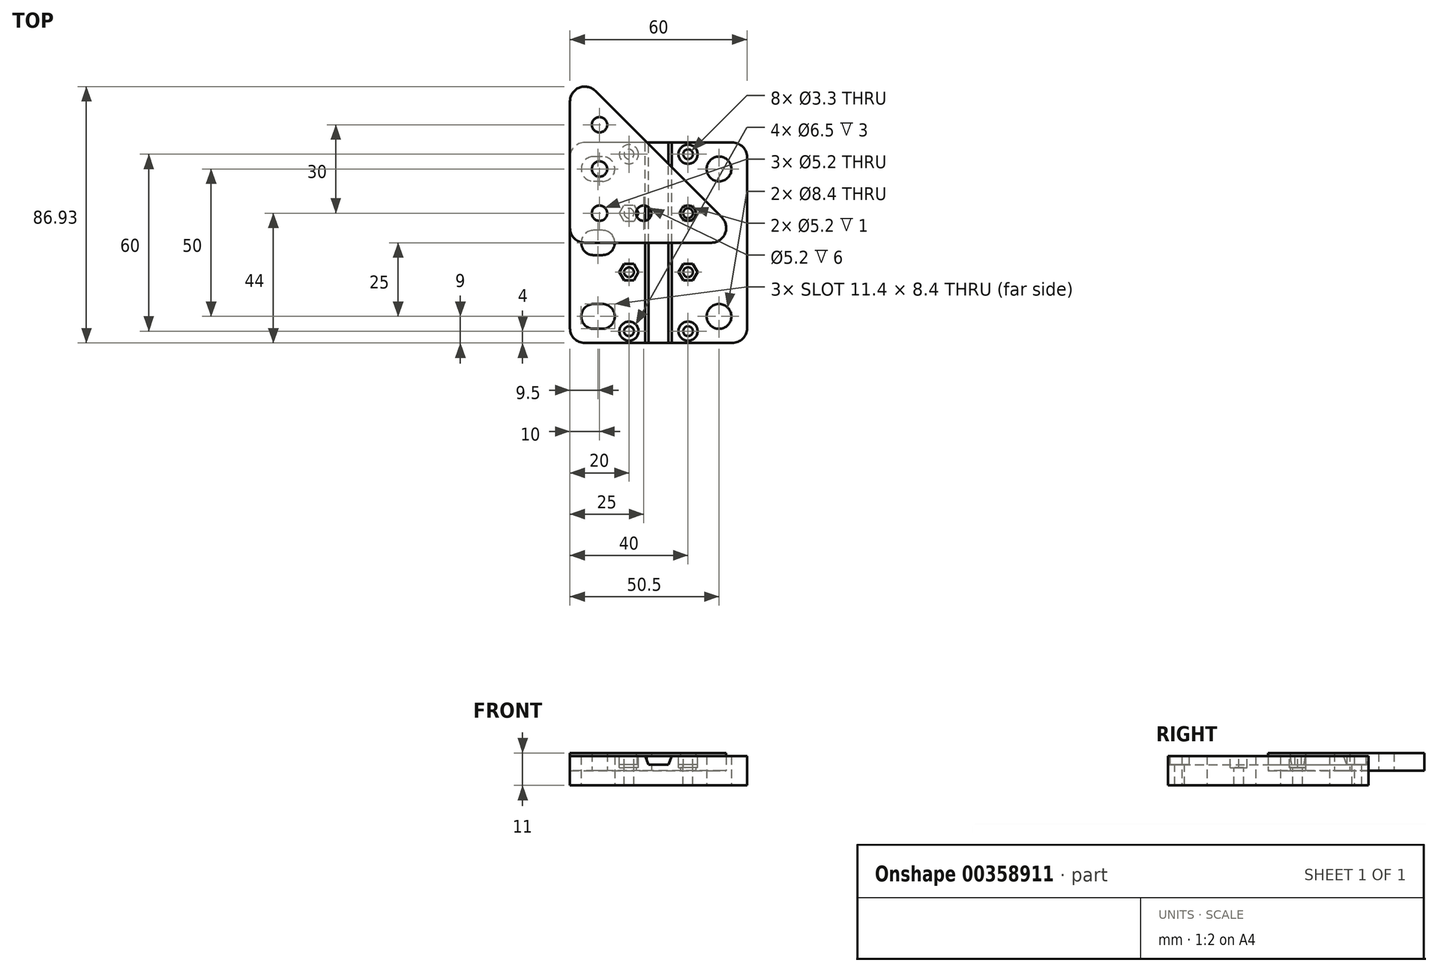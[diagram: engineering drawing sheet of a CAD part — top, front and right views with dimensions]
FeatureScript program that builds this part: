
annotation { "Feature Type Name" : "Feature", "Feature Type Description" : "" }
export const myFeature = defineFeature(function(context is Context, id is Id, definition is map)
    precondition{}
    {
        {
            var Q0;
            Q0=qCreatedBy(makeId("Top.planeOp"),FACE);
            var sketch = newSketch(context, id + "F0", { "sketchPlane" : qUnion([Q0])});
            skLineSegment(sketch, "E0", {"start": v(-30, 0) * mm, "end": v(30, 0) * mm});
            skLineSegment(sketch, "E1", {"start": v(30, 0) * mm, "end": v(-30, 60) * mm});
            skLineSegment(sketch, "E2", {"start": v(-30, 60) * mm, "end": v(-30, 0) * mm});
            skCircle(sketch, "E3", {"center": v(-20, 10) * mm, "radius": 2.6 * mm});
            skCircle(sketch, "E4.0.1.0", {"center": v(-20, 25) * mm, "radius": 2.6 * mm});
            skCircle(sketch, "E4.0.2.0", {"center": v(-20, 40) * mm, "radius": 2.6 * mm});
            skCircle(sketch, "E4.1.0.0", {"center": v(-5, 10) * mm, "radius": 2.6 * mm});
            skCircle(sketch, "E4.2.0.0", {"center": v(10, 10) * mm, "radius": 2.6 * mm});
            skLineSegment(sketch, "E4.direction1", {"start": v(-20, 10) * mm, "end": v(-5, 10) * mm, "construction": true});
            skLineSegment(sketch, "E4.direction2", {"start": v(-20, 10) * mm, "end": v(-20, 25) * mm, "construction": true});
            skLineSegment(sketch, "E5", {"start": v(-20, 10) * mm, "end": v(-30, 10) * mm, "construction": true});
            skLineSegment(sketch, "E6", {"start": v(-20, 10) * mm, "end": v(-20, 0) * mm, "construction": true});
            skSolve(sketch);
        }
        {
            var Q0;
            Q0=makeQuery(id+"F0.imprint","IMPRINT",FACE,{"disambiguationData":[TD([[makeQuery(id+"F0.imprint","IMPRINT",EDGE,{"derivedFrom":sQuery(id+"F0.wireOp",EDGE,"E0")}),1.0]])]});
            extrude(context, id + "F1", {"entities" : qUnion([Q0]), "depth" : 6 * mm});
        }
        {
            var Q0;
            Q0=makeQuery(id+"F1.opExtrude","SWEPT_EDGE",EDGE,{"disambiguationData":[OSD([sQuery(id+"F0.wireOp",EDGE,"E0"),sQuery(id+"F0.wireOp",EDGE,"E2")])]});
            var Q1;
            Q1=makeQuery(id+"F1.opExtrude","SWEPT_EDGE",EDGE,{"disambiguationData":[OSD([sQuery(id+"F0.wireOp",EDGE,"E0"),sQuery(id+"F0.wireOp",EDGE,"E1")])]});
            var Q2;
            Q2=makeQuery(id+"F1.opExtrude","SWEPT_EDGE",EDGE,{"disambiguationData":[OSD([sQuery(id+"F0.wireOp",EDGE,"E1"),sQuery(id+"F0.wireOp",EDGE,"E2")])]});
            fillet(context, id + "F2", {"entities" : qUnion([Q0, Q1, Q2]), "radius" : 5 * mm, "tangentPropagation" : true, "allowEdgeOverflow" : false});
        }
        {
            var Q0;
            Q0=qCreatedBy(makeId("Top.planeOp"),FACE);
            var sketch = newSketch(context, id + "F3", { "sketchPlane" : qUnion([Q0])});
            skLineSegment(sketch, "E7.bottom", {"start": v(30, 34) * mm, "end": v(-30, 34) * mm});
            skLineSegment(sketch, "E7.top", {"start": v(30, -34) * mm, "end": v(-30, -34) * mm});
            skLineSegment(sketch, "E7.left", {"start": v(30, 34) * mm, "end": v(30, -34) * mm});
            skLineSegment(sketch, "E7.right", {"start": v(-30, 34) * mm, "end": v(-30, -34) * mm});
            skPoint(sketch, "E7.middle", {"position": v(0, 0) * mm});
            skPoint(sketch, "E8.middle", {"position": v(-30, 34) * mm});
            skCircle(sketch, "E9", {"center": v(20.5, 0) * mm, "radius": 11 * mm, "construction": true});
            skLineSegment(sketch, "E10", {"start": v(20.5, -34) * mm, "end": v(20.5, 34) * mm, "construction": true});
            skCircle(sketch, "E11", {"center": v(20.5, 25) * mm, "radius": 4.2 * mm});
            skCircle(sketch, "E12.0.1.0", {"center": v(20.5, -25) * mm, "radius": 4.2 * mm});
            skLineSegment(sketch, "E12.direction1", {"start": v(20.5, 25) * mm, "end": v(-14.9, 25) * mm, "construction": true});
            skLineSegment(sketch, "E12.direction2", {"start": v(20.5, 25) * mm, "end": v(20.5, -25) * mm, "construction": true});
            skLineSegment(sketch, "E13", {"start": v(-20.5, 34) * mm, "end": v(-20.5, -34) * mm, "construction": true});
            skLineSegment(sketch, "E14.bottom", {"start": v(-19, -29.2) * mm, "end": v(-22, -29.2) * mm});
            skLineSegment(sketch, "E14.top", {"start": v(-19, -20.8) * mm, "end": v(-22, -20.8) * mm});
            skLineSegment(sketch, "E14.left", {"start": v(-19, -29.2) * mm, "end": v(-19, -20.8) * mm});
            skLineSegment(sketch, "E14.right", {"start": v(-22, -29.2) * mm, "end": v(-22, -20.8) * mm});
            skPoint(sketch, "E14.middle", {"position": v(-20.5, -25) * mm});
            skArc(sketch, "E15", {"start": v(-22, -29.2) * mm, "mid": v(-26.2, -25) * mm, "end": v(-22, -20.8) * mm});
            skArc(sketch, "E16", {"start": v(-19, -29.2) * mm, "mid": v(-14.8, -25) * mm, "end": v(-19, -20.8) * mm});
            skLineSegment(sketch, "E17.0.1.0", {"start": v(-19, -4.2) * mm, "end": v(-22, -4.2) * mm});
            skLineSegment(sketch, "E17.0.1.1", {"start": v(-19, 4.2) * mm, "end": v(-22, 4.2) * mm});
            skArc(sketch, "E17.0.1.2", {"start": v(-19, -4.2) * mm, "mid": v(-14.8, 0) * mm, "end": v(-19, 4.2) * mm});
            skArc(sketch, "E17.0.1.3", {"start": v(-22, -4.2) * mm, "mid": v(-26.2, 0) * mm, "end": v(-22, 4.2) * mm});
            skLineSegment(sketch, "E17.0.1.4", {"start": v(-22, -4.2) * mm, "end": v(-22, 4.2) * mm});
            skLineSegment(sketch, "E17.0.1.5", {"start": v(-19, -4.2) * mm, "end": v(-19, 4.2) * mm});
            skPoint(sketch, "E17.0.1.6", {"position": v(-20.5, 0) * mm});
            skLineSegment(sketch, "E17.0.2.0", {"start": v(-19, 20.8) * mm, "end": v(-22, 20.8) * mm});
            skLineSegment(sketch, "E17.0.2.1", {"start": v(-19, 29.2) * mm, "end": v(-22, 29.2) * mm});
            skArc(sketch, "E17.0.2.2", {"start": v(-19, 20.8) * mm, "mid": v(-14.8, 25) * mm, "end": v(-19, 29.2) * mm});
            skArc(sketch, "E17.0.2.3", {"start": v(-22, 20.8) * mm, "mid": v(-26.2, 25) * mm, "end": v(-22, 29.2) * mm});
            skLineSegment(sketch, "E17.0.2.4", {"start": v(-22, 20.8) * mm, "end": v(-22, 29.2) * mm});
            skLineSegment(sketch, "E17.0.2.5", {"start": v(-19, 20.8) * mm, "end": v(-19, 29.2) * mm});
            skPoint(sketch, "E17.0.2.6", {"position": v(-20.5, 25) * mm});
            skLineSegment(sketch, "E17.direction1", {"start": v(-22, -29.2) * mm, "end": v(3.25, -29.2) * mm, "construction": true});
            skLineSegment(sketch, "E17.direction2", {"start": v(-22, -29.2) * mm, "end": v(-22, -4.2) * mm, "construction": true});
            skSolve(sketch);
        }
        {
            var Q0;
            Q0=makeQuery(id+"F3.imprint","IMPRINT",FACE,{"disambiguationData":[TD([[makeQuery(id+"F3.imprint","IMPRINT",EDGE,{"derivedFrom":sQuery(id+"F3.wireOp",EDGE,"E7.bottom")}),1.0]])]});
            extrude(context, id + "F4", {"entities" : qUnion([Q0]), "endBound" : BoundingType.SYMMETRIC, "depth" : 10 * mm});
        }
        {
            var Q0;
            Q0=makeQuery(id+"F4.opExtrude","SWEPT_EDGE",EDGE,{"disambiguationData":[OSD([sQuery(id+"F3.wireOp",EDGE,"E7.bottom"),sQuery(id+"F3.wireOp",EDGE,"E7.right")])]});
            var Q1;
            Q1=makeQuery(id+"F4.opExtrude","SWEPT_EDGE",EDGE,{"disambiguationData":[OSD([sQuery(id+"F3.wireOp",EDGE,"E7.top"),sQuery(id+"F3.wireOp",EDGE,"E7.right")])]});
            var Q2;
            Q2=makeQuery(id+"F4.opExtrude","SWEPT_EDGE",EDGE,{"disambiguationData":[OSD([sQuery(id+"F3.wireOp",EDGE,"E7.top"),sQuery(id+"F3.wireOp",EDGE,"E7.left")])]});
            var Q3;
            Q3=makeQuery(id+"F4.opExtrude","SWEPT_EDGE",EDGE,{"disambiguationData":[OSD([sQuery(id+"F3.wireOp",EDGE,"E7.bottom"),sQuery(id+"F3.wireOp",EDGE,"E7.left")])]});
            fillet(context, id + "F5", {"entities" : qUnion([Q0, Q1, Q2, Q3]), "radius" : 5 * mm, "tangentPropagation" : true, "allowEdgeOverflow" : false});
        }
        {
            var Q0;
            Q0=makeQuery(id+"F4.opExtrude","CAP_FACE",FACE,{"disambiguationData":[OSD([sQuery(id+"F3.wireOp",EDGE,"E7.bottom"),sQuery(id+"F3.wireOp",EDGE,"E7.top"),sQuery(id+"F3.wireOp",EDGE,"E7.left"),sQuery(id+"F3.wireOp",EDGE,"E7.right"),sQuery(id+"F3.wireOp",EDGE,"E11"),sQuery(id+"F3.wireOp",EDGE,"E12.0.1.0"),sQuery(id+"F3.wireOp",EDGE,"E14.bottom"),sQuery(id+"F3.wireOp",EDGE,"E14.top"),sQuery(id+"F3.wireOp",EDGE,"E15"),sQuery(id+"F3.wireOp",EDGE,"E16"),sQuery(id+"F3.wireOp",EDGE,"E17.0.1.0"),sQuery(id+"F3.wireOp",EDGE,"E17.0.1.1"),sQuery(id+"F3.wireOp",EDGE,"E17.0.1.2"),sQuery(id+"F3.wireOp",EDGE,"E17.0.1.3"),sQuery(id+"F3.wireOp",EDGE,"E17.0.2.0"),sQuery(id+"F3.wireOp",EDGE,"E17.0.2.1"),sQuery(id+"F3.wireOp",EDGE,"E17.0.2.2"),sQuery(id+"F3.wireOp",EDGE,"E17.0.2.3")])],"isStart":false});
            var sketch = newSketch(context, id + "F6", { "sketchPlane" : qUnion([Q0])});
            skCircle(sketch, "E18", {"center": v(-10, -30) * mm, "radius": 1.6 * mm});
            skCircle(sketch, "E19.0.1.0", {"center": v(-10, 30) * mm, "radius": 1.6 * mm});
            skCircle(sketch, "E19.1.0.0", {"center": v(10, -30) * mm, "radius": 1.6 * mm});
            skCircle(sketch, "E19.1.1.0", {"center": v(10, 30) * mm, "radius": 1.6 * mm});
            skLineSegment(sketch, "E19.direction1", {"start": v(-10, -30) * mm, "end": v(10, -30) * mm, "construction": true});
            skLineSegment(sketch, "E19.direction2", {"start": v(-10, -30) * mm, "end": v(-10, 30) * mm, "construction": true});
            skSolve(sketch);
        }
        {
            var Q0;
            Q0=sQuery(id+"F6.wireOp",VERTEX,"E19.0.1.0.center");
            var Q1;
            Q1=sQuery(id+"F6.wireOp",VERTEX,"E19.1.1.0.center");
            var Q2;
            Q2=sQuery(id+"F6.wireOp",VERTEX,"E18.center");
            var Q3;
            Q3=sQuery(id+"F6.wireOp",VERTEX,"E19.1.0.0.center");
            var Q4;
            Q4=makeQuery(id+"F4.opExtrude","SWEPT_BODY",BODY,{"disambiguationData":[OSD([sQuery(id+"F3.wireOp",EDGE,"E7.bottom"),sQuery(id+"F3.wireOp",EDGE,"E7.top"),sQuery(id+"F3.wireOp",EDGE,"E7.left"),sQuery(id+"F3.wireOp",EDGE,"E7.right"),sQuery(id+"F3.wireOp",EDGE,"E11"),sQuery(id+"F3.wireOp",EDGE,"E12.0.1.0"),sQuery(id+"F3.wireOp",EDGE,"E14.bottom"),sQuery(id+"F3.wireOp",EDGE,"E14.top"),sQuery(id+"F3.wireOp",EDGE,"E15"),sQuery(id+"F3.wireOp",EDGE,"E16"),sQuery(id+"F3.wireOp",EDGE,"E17.0.1.0"),sQuery(id+"F3.wireOp",EDGE,"E17.0.1.1"),sQuery(id+"F3.wireOp",EDGE,"E17.0.1.2"),sQuery(id+"F3.wireOp",EDGE,"E17.0.1.3"),sQuery(id+"F3.wireOp",EDGE,"E17.0.2.0"),sQuery(id+"F3.wireOp",EDGE,"E17.0.2.1"),sQuery(id+"F3.wireOp",EDGE,"E17.0.2.2"),sQuery(id+"F3.wireOp",EDGE,"E17.0.2.3")])]});
            hole(context, id + "F7", {"style" : HoleStyle.C_BORE, "endStyle" : HoleEndStyle.THROUGH, "standardTappedOrClearance" : lookupTablePath({ "standard" : "ISO", "fit" : "Normal", "size" : "M3", "type" : "Clearance" }), "standardBlindInLast" : lookupTablePath({ "fit" : "Standard", "standard" : "ISO", "size" : "M3", "type" : "Clearance" }), "holeDiameter" : 3.3 * mm, "cBoreDiameter" : 6.5 * mm, "cBoreDepth" : 3 * mm, "isTappedThrough" : true, "tappedDepth" : 12 * mm, "tapClearance" : 3, "startFromSketch" : true, "locations" : qUnion([Q0, Q1, Q2, Q3]), "scope" : qUnion([Q4])});
        }
        {
            var Q0;
            Q0=makeQuery(id+"F4.opExtrude","CAP_FACE",FACE,{"disambiguationData":[OSD([sQuery(id+"F3.wireOp",EDGE,"E7.bottom"),sQuery(id+"F3.wireOp",EDGE,"E7.top"),sQuery(id+"F3.wireOp",EDGE,"E7.left"),sQuery(id+"F3.wireOp",EDGE,"E7.right"),sQuery(id+"F3.wireOp",EDGE,"E11"),sQuery(id+"F3.wireOp",EDGE,"E12.0.1.0"),sQuery(id+"F3.wireOp",EDGE,"E14.bottom"),sQuery(id+"F3.wireOp",EDGE,"E14.top"),sQuery(id+"F3.wireOp",EDGE,"E15"),sQuery(id+"F3.wireOp",EDGE,"E16"),sQuery(id+"F3.wireOp",EDGE,"E17.0.1.0"),sQuery(id+"F3.wireOp",EDGE,"E17.0.1.1"),sQuery(id+"F3.wireOp",EDGE,"E17.0.1.2"),sQuery(id+"F3.wireOp",EDGE,"E17.0.1.3"),sQuery(id+"F3.wireOp",EDGE,"E17.0.2.0"),sQuery(id+"F3.wireOp",EDGE,"E17.0.2.1"),sQuery(id+"F3.wireOp",EDGE,"E17.0.2.2"),sQuery(id+"F3.wireOp",EDGE,"E17.0.2.3")])],"isStart":false});
            var sketch = newSketch(context, id + "F8", { "sketchPlane" : qUnion([Q0])});
            skCircle(sketch, "E20.cCircle", {"center": v(-10, -10) * mm, "radius": 3.25 * mm, "construction": true});
            skLineSegment(sketch, "E20.0", {"start": v(-6.75, -10) * mm, "end": v(-8.38, -12.81) * mm});
            skLineSegment(sketch, "E20.1", {"start": v(-8.38, -12.81) * mm, "end": v(-11.62, -12.81) * mm});
            skLineSegment(sketch, "E20.2", {"start": v(-11.62, -12.81) * mm, "end": v(-13.25, -10) * mm});
            skLineSegment(sketch, "E20.3", {"start": v(-13.25, -10) * mm, "end": v(-11.62, -7.19) * mm});
            skLineSegment(sketch, "E20.4", {"start": v(-11.62, -7.19) * mm, "end": v(-8.37, -7.19) * mm});
            skLineSegment(sketch, "E20.5", {"start": v(-8.37, -7.19) * mm, "end": v(-6.75, -10) * mm});
            skLineSegment(sketch, "E21.0.1.0", {"start": v(-13.25, 10) * mm, "end": v(-11.62, 12.81) * mm});
            skLineSegment(sketch, "E21.0.1.1", {"start": v(-11.62, 7.19) * mm, "end": v(-13.25, 10) * mm});
            skLineSegment(sketch, "E21.0.1.2", {"start": v(-8.38, 7.19) * mm, "end": v(-11.62, 7.19) * mm});
            skLineSegment(sketch, "E21.0.1.3", {"start": v(-6.75, 10) * mm, "end": v(-8.38, 7.19) * mm});
            skCircle(sketch, "E21.0.1.4", {"center": v(-10, 10) * mm, "radius": 3.25 * mm, "construction": true});
            skLineSegment(sketch, "E21.0.1.5", {"start": v(-8.37, 12.81) * mm, "end": v(-6.75, 10) * mm});
            skLineSegment(sketch, "E21.0.1.6", {"start": v(-11.62, 12.81) * mm, "end": v(-8.37, 12.81) * mm});
            skLineSegment(sketch, "E21.1.0.0", {"start": v(6.75, -10) * mm, "end": v(8.38, -7.19) * mm});
            skLineSegment(sketch, "E21.1.0.1", {"start": v(8.38, -12.81) * mm, "end": v(6.75, -10) * mm});
            skLineSegment(sketch, "E21.1.0.2", {"start": v(11.62, -12.81) * mm, "end": v(8.38, -12.81) * mm});
            skLineSegment(sketch, "E21.1.0.3", {"start": v(13.25, -10) * mm, "end": v(11.62, -12.81) * mm});
            skCircle(sketch, "E21.1.0.4", {"center": v(10, -10) * mm, "radius": 3.25 * mm, "construction": true});
            skLineSegment(sketch, "E21.1.0.5", {"start": v(11.63, -7.19) * mm, "end": v(13.25, -10) * mm});
            skLineSegment(sketch, "E21.1.0.6", {"start": v(8.38, -7.19) * mm, "end": v(11.63, -7.19) * mm});
            skLineSegment(sketch, "E21.1.1.0", {"start": v(6.75, 10) * mm, "end": v(8.38, 12.81) * mm});
            skLineSegment(sketch, "E21.1.1.1", {"start": v(8.38, 7.19) * mm, "end": v(6.75, 10) * mm});
            skLineSegment(sketch, "E21.1.1.2", {"start": v(11.62, 7.19) * mm, "end": v(8.38, 7.19) * mm});
            skLineSegment(sketch, "E21.1.1.3", {"start": v(13.25, 10) * mm, "end": v(11.62, 7.19) * mm});
            skCircle(sketch, "E21.1.1.4", {"center": v(10, 10) * mm, "radius": 3.25 * mm, "construction": true});
            skLineSegment(sketch, "E21.1.1.5", {"start": v(11.63, 12.81) * mm, "end": v(13.25, 10) * mm});
            skLineSegment(sketch, "E21.1.1.6", {"start": v(8.38, 12.81) * mm, "end": v(11.63, 12.81) * mm});
            skLineSegment(sketch, "E21.direction1", {"start": v(-11.62, -12.81) * mm, "end": v(8.38, -12.81) * mm, "construction": true});
            skLineSegment(sketch, "E21.direction2", {"start": v(-11.62, -12.81) * mm, "end": v(-11.62, 7.19) * mm, "construction": true});
            skSolve(sketch);
        }
        {
            var Q0;
            Q0=makeQuery(id+"F8.imprint","IMPRINT",FACE,{"disambiguationData":[TD([[makeQuery(id+"F8.imprint","IMPRINT",EDGE,{"derivedFrom":sQuery(id+"F8.wireOp",EDGE,"E21.0.1.0")}),-1.0]])]});
            var Q1;
            Q1=makeQuery(id+"F8.imprint","IMPRINT",FACE,{"disambiguationData":[TD([[makeQuery(id+"F8.imprint","IMPRINT",EDGE,{"derivedFrom":sQuery(id+"F8.wireOp",EDGE,"E21.1.1.0")}),-1.0]])]});
            var Q2;
            Q2=makeQuery(id+"F8.imprint","IMPRINT",FACE,{"disambiguationData":[TD([[makeQuery(id+"F8.imprint","IMPRINT",EDGE,{"derivedFrom":sQuery(id+"F8.wireOp",EDGE,"E20.0")}),-1.0]])]});
            var Q3;
            Q3=makeQuery(id+"F8.imprint","IMPRINT",FACE,{"disambiguationData":[TD([[makeQuery(id+"F8.imprint","IMPRINT",EDGE,{"derivedFrom":sQuery(id+"F8.wireOp",EDGE,"E21.1.0.0")}),-1.0]])]});
            extrude(context, id + "F9", {"entities" : qUnion([Q0, Q1, Q2, Q3]), "operationType" : NewBodyOperationType.REMOVE, "oppositeDirection" : true, "depth" : 4 * mm});
        }
        {
            var Q0;
            Q0=sQuery(id+"F8.wireOp",VERTEX,"E21.0.1.4.center");
            var Q1;
            Q1=sQuery(id+"F8.wireOp",VERTEX,"E21.1.1.4.center");
            var Q2;
            Q2=sQuery(id+"F8.wireOp",VERTEX,"E20.cCircle.center");
            var Q3;
            Q3=sQuery(id+"F8.wireOp",VERTEX,"E21.1.0.4.center");
            var Q4;
            Q4=makeQuery(id+"F4.opExtrude","SWEPT_BODY",BODY,{"disambiguationData":[OSD([sQuery(id+"F3.wireOp",EDGE,"E7.bottom"),sQuery(id+"F3.wireOp",EDGE,"E7.top"),sQuery(id+"F3.wireOp",EDGE,"E7.left"),sQuery(id+"F3.wireOp",EDGE,"E7.right"),sQuery(id+"F3.wireOp",EDGE,"E11"),sQuery(id+"F3.wireOp",EDGE,"E12.0.1.0"),sQuery(id+"F3.wireOp",EDGE,"E14.bottom"),sQuery(id+"F3.wireOp",EDGE,"E14.top"),sQuery(id+"F3.wireOp",EDGE,"E15"),sQuery(id+"F3.wireOp",EDGE,"E16"),sQuery(id+"F3.wireOp",EDGE,"E17.0.1.0"),sQuery(id+"F3.wireOp",EDGE,"E17.0.1.1"),sQuery(id+"F3.wireOp",EDGE,"E17.0.1.2"),sQuery(id+"F3.wireOp",EDGE,"E17.0.1.3"),sQuery(id+"F3.wireOp",EDGE,"E17.0.2.0"),sQuery(id+"F3.wireOp",EDGE,"E17.0.2.1"),sQuery(id+"F3.wireOp",EDGE,"E17.0.2.2"),sQuery(id+"F3.wireOp",EDGE,"E17.0.2.3")])]});
            hole(context, id + "F10", {"style" : HoleStyle.SIMPLE, "endStyle" : HoleEndStyle.THROUGH, "standardTappedOrClearance" : lookupTablePath({ "standard" : "ISO", "fit" : "Normal", "size" : "M3", "type" : "Clearance" }), "standardBlindInLast" : lookupTablePath({ "fit" : "Standard", "standard" : "ISO", "size" : "M3", "type" : "Clearance" }), "holeDiameter" : 3.3 * mm, "isTappedThrough" : true, "tappedDepth" : 12 * mm, "tapClearance" : 3, "startFromSketch" : true, "locations" : qUnion([Q0, Q1, Q2, Q3]), "scope" : qUnion([Q4])});
        }
        {
            var Q0;
            Q0=makeQuery(id+"F4.opExtrude","SWEPT_FACE",FACE,{"disambiguationData":[OSD([sQuery(id+"F3.wireOp",EDGE,"E7.bottom")])]});
            var sketch = newSketch(context, id + "F11", { "sketchPlane" : qUnion([Q0])});
            skPoint(sketch, "E22.middle", {"position": v(0, 0) * mm});
            skLineSegment(sketch, "E23", {"start": v(-4.5, 5) * mm, "end": v(4.5, 5) * mm});
            skLineSegment(sketch, "E24", {"start": v(4.5, 5) * mm, "end": v(3.4, 2) * mm});
            skLineSegment(sketch, "E25", {"start": v(3.4, 2) * mm, "end": v(-3.4, 2) * mm});
            skLineSegment(sketch, "E26", {"start": v(-3.4, 2) * mm, "end": v(-4.5, 5) * mm});
            skSolve(sketch);
        }
        {
            var Q0;
            Q0=makeQuery(id+"F11.imprint","IMPRINT",FACE,{"disambiguationData":[TD([[makeQuery(id+"F11.imprint","IMPRINT",EDGE,{"derivedFrom":sQuery(id+"F11.wireOp",EDGE,"E23")}),-1.0]])]});
            extrude(context, id + "F12", {"entities" : qUnion([Q0]), "operationType" : NewBodyOperationType.REMOVE, "oppositeDirection" : true, "depth" : 3 * mm, "hasDraft" : true, "draftAngle" : 20 * degree, "draftPullDirection" : true});
        }
        {
            var Q0;
            Q0=makeQuery(id+"F11.imprint","IMPRINT",FACE,{"disambiguationData":[TD([[makeQuery(id+"F11.imprint","IMPRINT",EDGE,{"derivedFrom":sQuery(id+"F11.wireOp",EDGE,"E23")}),-1.0]])]});
            extrude(context, id + "F13", {"entities" : qUnion([Q0]), "operationType" : NewBodyOperationType.REMOVE, "endBound" : BoundingType.THROUGH_ALL, "oppositeDirection" : true, "depth" : 25 * mm});
        }
    });
